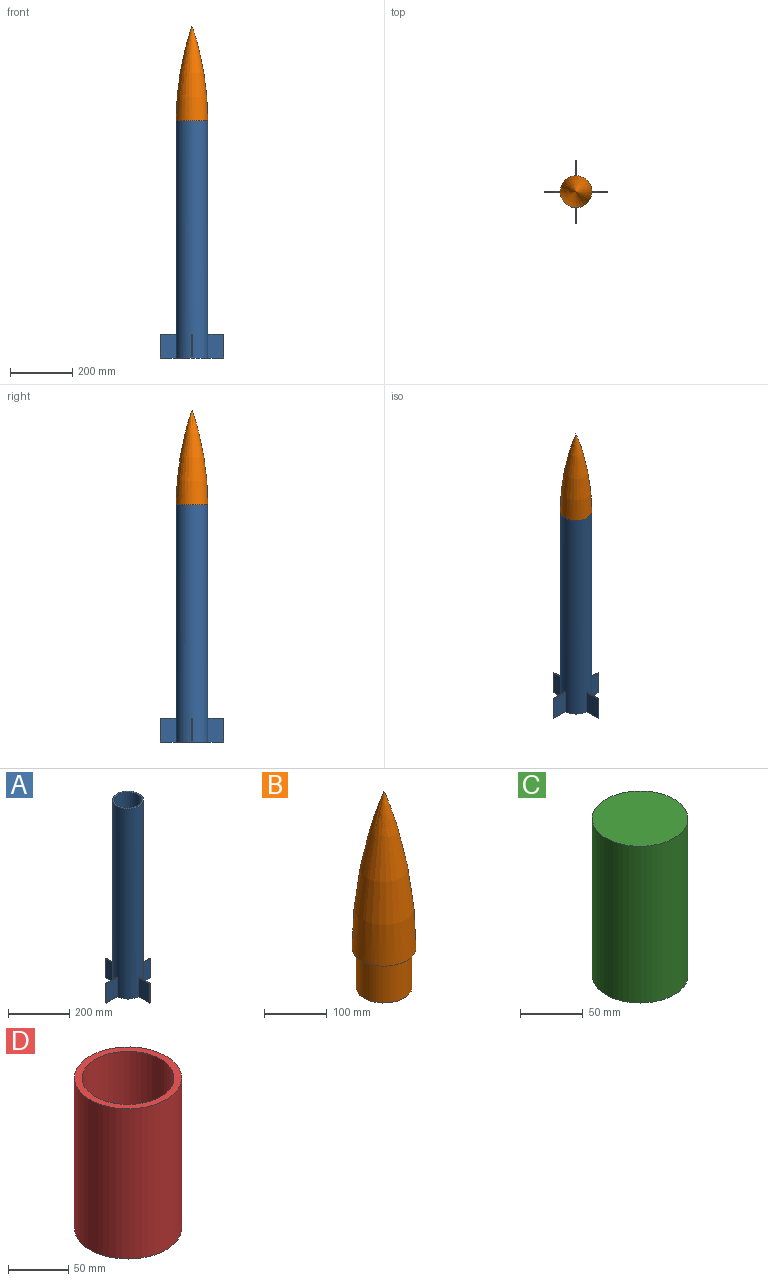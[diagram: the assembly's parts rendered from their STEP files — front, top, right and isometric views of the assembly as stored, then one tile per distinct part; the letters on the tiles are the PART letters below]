
ASSEMBLY  parts=4 mates=3
PART A: 20 faces, bbox 203.2x203.2x762 mm
  f0: cylinder r=50.8mm len=762mm, axis (0,0,-1), area 242251.7mm2, adj f1,f2,f3,f4,f6,f8,f9,f10
  f1: plane 101.6x101.6mm, normal (0,0,1), area 1900.2mm2, adj f0,f19
  f2: plane 203.2x203.2mm, normal (0,0,-1), area 2545.4mm2, adj f0,f3,f4,f5,f7,f8,f9,f11
  f3: plane 76.2x50.83mm, normal (0,1,0), area 3872.9mm2, adj f0,f2,f5,f6
  f4: plane 76.2x50.83mm, normal (0,-1,0), area 3872.9mm2, adj f0,f2,f5,f6
  f5: plane 76.2x3.18mm, normal (1,0,0), area 241.9mm2, adj f2,f3,f4,f6
  f6: plane 50.83x3.18mm, normal (0,0,1), area 161.3mm2, adj f0,f3,f4,f5
  f7: plane 76.2x3.18mm, normal (-1,0,0), area 241.9mm2, adj f2,f8,f9,f10
  f8: plane 76.2x50.83mm, normal (0,-1,0), area 3872.9mm2, adj f0,f2,f7,f10
  f9: plane 76.2x50.83mm, normal (0,1,0), area 3872.9mm2, adj f0,f2,f7,f10
  f10: plane 50.83x3.18mm, normal (0,0,1), area 161.3mm2, adj f0,f7,f8,f9
  f11: plane 76.2x50.83mm, normal (-1,0,0), area 3872.9mm2, adj f0,f2,f13,f14
  f12: plane 76.2x50.83mm, normal (1,0,0), area 3872.9mm2, adj f0,f2,f13,f14
  f13: plane 76.2x3.18mm, normal (0,1,0), area 241.9mm2, adj f2,f11,f12,f14
  f14: plane 50.83x3.18mm, normal (0,0,1), area 161.3mm2, adj f0,f11,f12,f13
  f15: plane 76.2x50.83mm, normal (-1,0,0), area 3872.9mm2, adj f0,f2,f16,f18
  f16: plane 76.2x3.18mm, normal (0,-1,0), area 241.9mm2, adj f2,f15,f17,f18
  f17: plane 76.2x50.83mm, normal (1,0,0), area 3872.9mm2, adj f0,f2,f16,f18
  f18: plane 50.83x3.18mm, normal (0,0,1), area 161.3mm2, adj f0,f15,f16,f17
  f19: cylinder r=44.45mm len=762mm, axis (0,0,-1), area 212817.1mm2, adj f1,f2
PART B: 4 faces, bbox 101.6x101.6x381 mm
  f0: plane 101.6x101.6mm, normal (0,0,-1), area 1900.2mm2, adj f1,f2
  f1: revolved ~304.8x101.6mm, area 65932.5mm2, adj f0
  f2: cylinder r=44.45mm len=88.9mm, axis (0,0,1), area 21281.7mm2, adj f0,f3
  f3: plane 88.9x88.9mm, normal (0,0,-1), area 6207.2mm2, adj f2
PART C: 6 faces, bbox 76.2x76.2x152.4 mm
  f0: cylinder r=38.1mm len=152.4mm, axis (0,0,1), area 36482.9mm2, adj f1,f5
  f1: plane 76.2x76.2mm, normal (0,0,1), area 4560.4mm2, adj f0
  f2: plane 12.7x12.7mm, normal (0,0,-1), area 126.7mm2, adj f3
  f3: cylinder r=6.35mm len=120.65mm, axis (0,0,1), area 4813.7mm2, adj f2,f4
  f4: cone r=6.35mm half-angle=19.5deg, axis (0,0,-1), area 1140.1mm2, adj f3,f5
  f5: plane 76.2x76.2mm, normal (0,0,-1), area 4053.7mm2, adj f0,f4
PART D: 4 faces, bbox 88.9x88.9x152.4 mm
  f0: cylinder r=44.45mm len=152.4mm, axis (0,0,1), area 42563.4mm2, adj f1,f3
  f1: plane 88.9x88.9mm, normal (0,0,1), area 1646.8mm2, adj f0,f2
  f2: cylinder r=38.1mm len=152.4mm, axis (0,0,1), area 36482.9mm2, adj f1,f3
  f3: plane 88.9x88.9mm, normal (0,0,-1), area 1646.8mm2, adj f0,f2
PLACE A at identity fixed
PLACE B at identity
PLACE C t=(0,0,101.6)mm
PLACE D t=(0,0,101.6)mm
MATE slider A.f19 <-> D.f0  axis (0,0,-1) through (0,0,0)mm
MATE fastened D.f0 <-> C.f0  axis (0,0,-1) through (0,0,25.4)mm
MATE slider B.f2 <-> A.f19  axis (0,0,-1) through (0,0,762)mm
